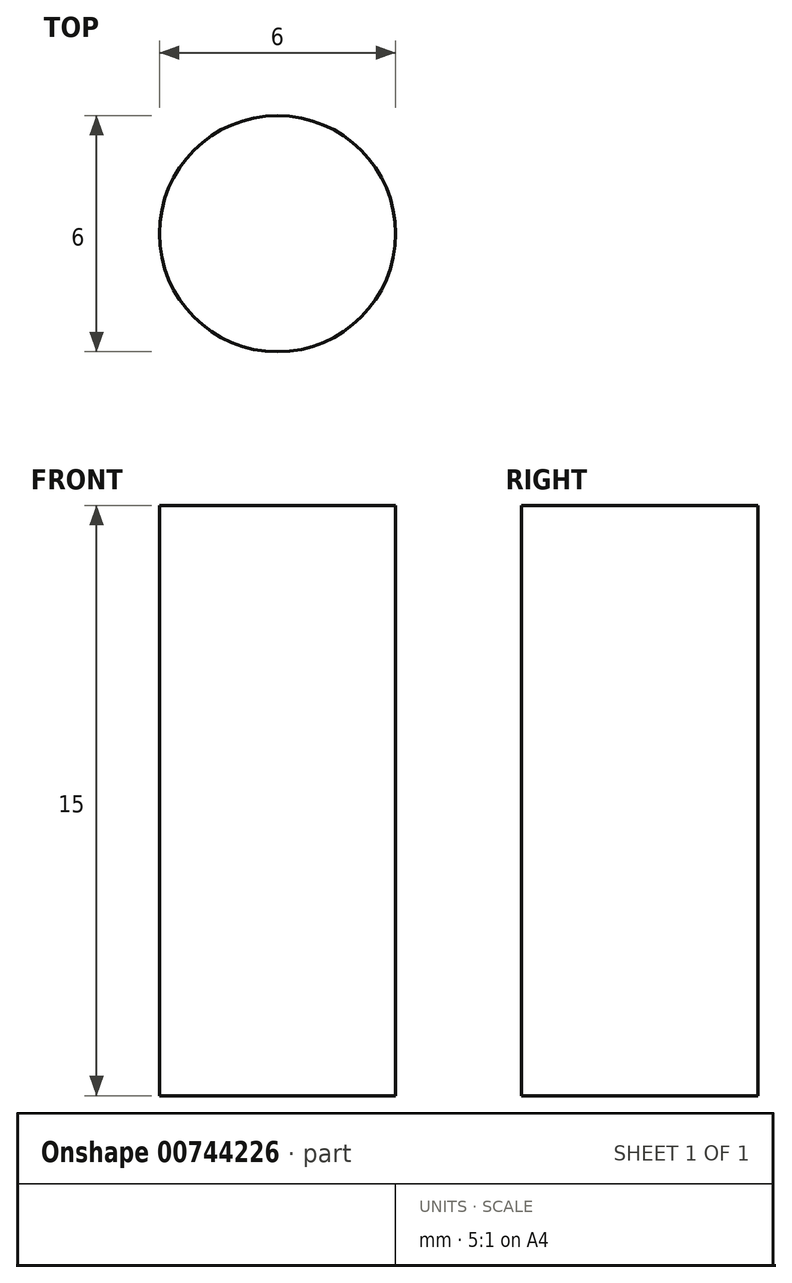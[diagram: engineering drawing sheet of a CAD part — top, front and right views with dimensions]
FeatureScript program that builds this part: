
annotation { "Feature Type Name" : "Feature", "Feature Type Description" : "" }
export const myFeature = defineFeature(function(context is Context, id is Id, definition is map)
    precondition{}
    {
        {
            var Q0;
            Q0=qCreatedBy(makeId("Top.planeOp"),FACE);
            var sketch = newSketch(context, id + "F0", { "sketchPlane" : qUnion([Q0])});
            skCircle(sketch, "E0", {"center": v(0, 0) * mm, "radius": 3 * mm});
            skSolve(sketch);
        }
        {
            var Q0;
            Q0=makeQuery(id+"F0.imprint","IMPRINT",FACE,{"disambiguationData":[TD([[makeQuery(id+"F0.imprint","IMPRINT",EDGE,{"derivedFrom":sQuery(id+"F0.wireOp",EDGE,"E0")}),1.0]])]});
            extrude(context, id + "F1", {"entities" : qUnion([Q0]), "depth" : 15 * mm, "offsetDistance" : 25 * mm});
        }
    });
